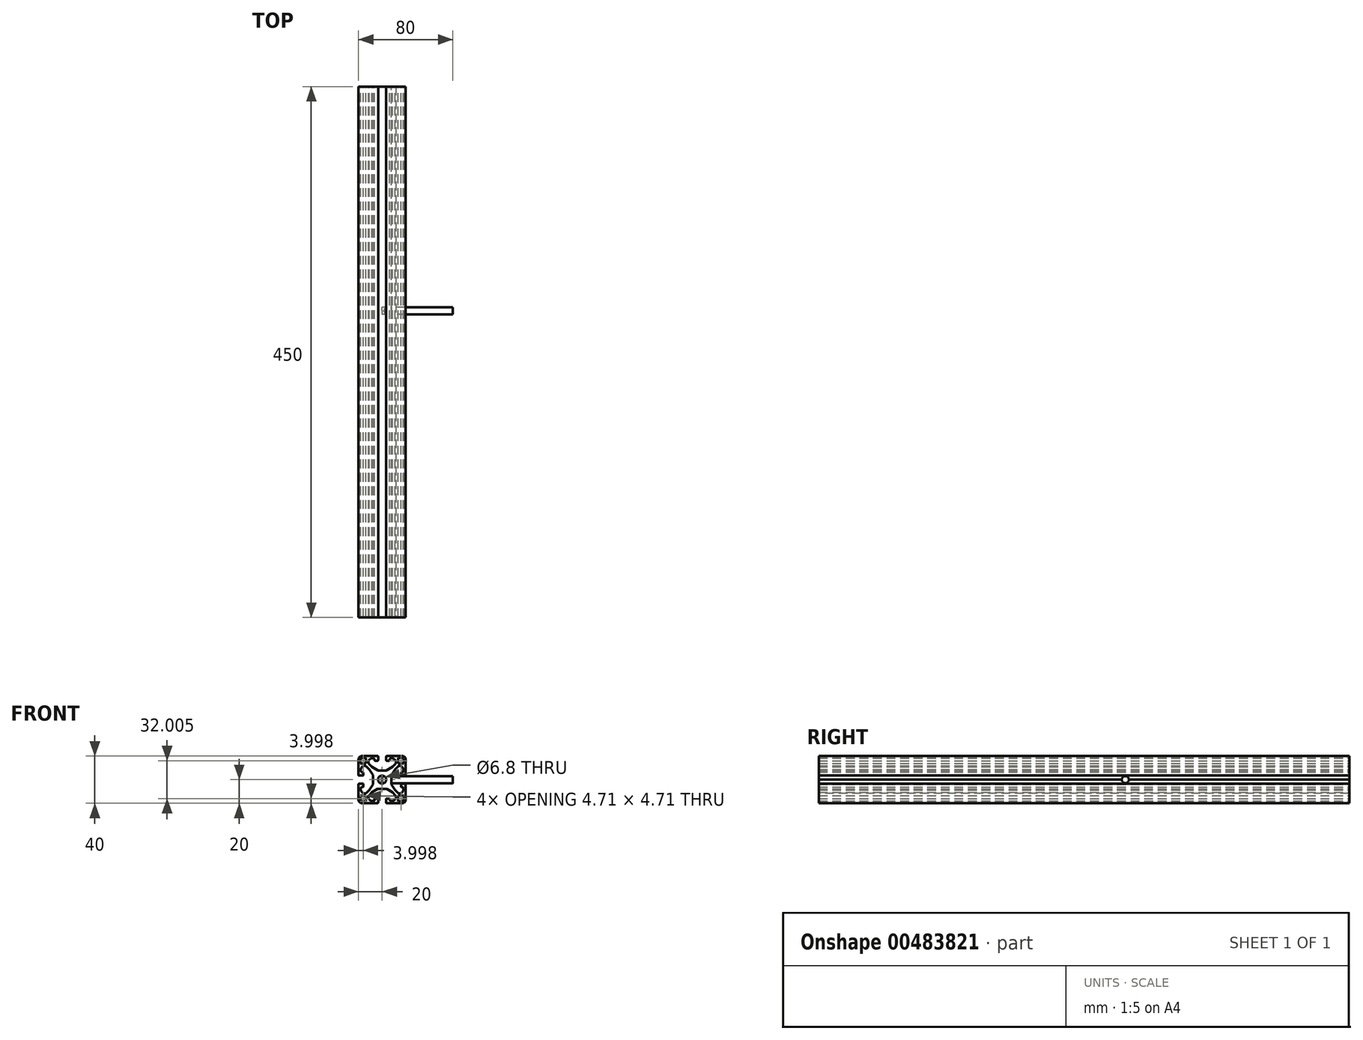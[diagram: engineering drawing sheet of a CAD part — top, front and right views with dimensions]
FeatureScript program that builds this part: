
annotation { "Feature Type Name" : "Feature", "Feature Type Description" : "" }
export const myFeature = defineFeature(function(context is Context, id is Id, definition is map)
    precondition{}
    {
        {
            var Q0;
            Q0=qCreatedBy(makeId("Front.planeOp"),FACE);
            var sketch = newSketch(context, id + "F0", { "sketchPlane" : qUnion([Q0])});
            skLineSegment(sketch, "E0.bottom", {"start": v(-16.36, 18.36) * mm, "end": v(-13.65, 18.36) * mm});
            skLineSegment(sketch, "E0.top", {"start": v(-18.36, 13.65) * mm, "end": v(-13.65, 13.65) * mm});
            skLineSegment(sketch, "E0.left", {"start": v(-18.36, 18.36) * mm, "end": v(-18.36, 18.36) * mm});
            skLineSegment(sketch, "E0.right", {"start": v(-13.65, 18.36) * mm, "end": v(-13.65, 13.65) * mm});
            skLineSegment(sketch, "E1", {"start": v(-7.83, 4) * mm, "end": v(-10.88, 8.69) * mm});
            skLineSegment(sketch, "E2", {"start": v(-10.88, 8.69) * mm, "end": v(-13.5, 11.3) * mm});
            skCircle(sketch, "E3", {"center": v(0, 0) * mm, "radius": 3.4 * mm});
            skLineSegment(sketch, "E4", {"start": v(-20, 3.4) * mm, "end": v(-19.97, 3.4) * mm});
            skLineSegment(sketch, "E5", {"start": v(-16, 3.9) * mm, "end": v(-16, 5.9) * mm});
            skLineSegment(sketch, "E6", {"start": v(-16.5, 6.4) * mm, "end": v(-17.08, 6.4) * mm});
            skFitSpline(sketch, "E7", {"points": [v(-18, 6.4) * mm, v(-18, 9.03) * mm, v(-17.04, 10.7) * mm, v(-15.02, 11.66) * mm, v(-13.85, 11.66) * mm, v(-51.55, 27.96) * mm, v(-53, 27.74) * mm], "startDerivative": vector(-2.1, 22.69) * mm, "endDerivative": vector(-5.98, -7.44) * mm});
            skArc(sketch, "E8.filletArc", {"start": v(-18.08, 7.34) * mm, "mid": v(-17.76, 6.67) * mm, "end": v(-17.08, 6.4) * mm});
            skArc(sketch, "E9.filletArc", {"start": v(-13.5, 11.3) * mm, "mid": v(-13.78, 11.5) * mm, "end": v(-14.1, 11.6) * mm});
            skLineSegment(sketch, "E10", {"start": v(-18.36, 16.36) * mm, "end": v(-18.36, 13.65) * mm});
            skPoint(sketch, "E11.visualSharp", {"position": v(-16, 6.4) * mm});
            skArc(sketch, "E11.filletArc", {"start": v(-16, 5.9) * mm, "mid": v(-16.15, 6.25) * mm, "end": v(-16.5, 6.4) * mm});
            skPoint(sketch, "E12.visualSharp", {"position": v(-16, 3.4) * mm});
            skArc(sketch, "E12.filletArc", {"start": v(-16.5, 3.4) * mm, "mid": v(-16.15, 3.55) * mm, "end": v(-16, 3.9) * mm});
            skLineSegment(sketch, "E13", {"start": v(-20, 3.9) * mm, "end": v(-20, 17) * mm});
            skArc(sketch, "E14.filletArc", {"start": v(-20, 3.9) * mm, "mid": v(-19.85, 3.55) * mm, "end": v(-19.5, 3.4) * mm});
            skLineSegment(sketch, "E15", {"start": v(-19.5, 3.4) * mm, "end": v(-16.5, 3.4) * mm});
            skPoint(sketch, "E16.visualSharp", {"position": v(-7.75, 3.88) * mm});
            skArc(sketch, "E16.filletArc", {"start": v(-7.75, 3.73) * mm, "mid": v(-7.77, 3.87) * mm, "end": v(-7.83, 4) * mm});
            skPoint(sketch, "E17.visualSharp", {"position": v(-18.36, 18.36) * mm});
            skArc(sketch, "E17.filletArc", {"start": v(-16.36, 18.36) * mm, "mid": v(-17.77, 17.77) * mm, "end": v(-18.36, 16.36) * mm});
            skPoint(sketch, "E18.visualSharp", {"position": v(-20, 20) * mm});
            skArc(sketch, "E18.filletArc", {"start": v(-17, 20) * mm, "mid": v(-19.12, 19.12) * mm, "end": v(-20, 17) * mm});
            skArc(sketch, "E19.MirrorCS", {"start": v(-7.34, 18.08) * mm, "mid": v(-6.67, 17.76) * mm, "end": v(-6.4, 17.08) * mm});
            skLineSegment(sketch, "E20.MirrorCS", {"start": v(-6.4, 16.5) * mm, "end": v(-6.4, 17.08) * mm});
            skLineSegment(sketch, "E21.MirrorCS", {"start": v(-3.9, 16) * mm, "end": v(-5.9, 16) * mm});
            skArc(sketch, "E22.MirrorCS", {"start": v(-5.9, 16) * mm, "mid": v(-6.25, 16.15) * mm, "end": v(-6.4, 16.5) * mm});
            skArc(sketch, "E23.MirrorCS", {"start": v(-11.3, 13.5) * mm, "mid": v(-11.5, 13.78) * mm, "end": v(-11.6, 14.1) * mm});
            skArc(sketch, "E24.MirrorCS", {"start": v(-3.73, 7.75) * mm, "mid": v(-3.87, 7.77) * mm, "end": v(-4, 7.83) * mm});
            skArc(sketch, "E25.MirrorCS", {"start": v(-3.4, 16.5) * mm, "mid": v(-3.55, 16.15) * mm, "end": v(-3.9, 16) * mm});
            skLineSegment(sketch, "E26.MirrorCS", {"start": v(-3.4, 19.5) * mm, "end": v(-3.4, 16.5) * mm});
            skLineSegment(sketch, "E27.MirrorCS", {"start": v(-3.4, 20) * mm, "end": v(-3.4, 19.97) * mm});
            skArc(sketch, "E28.MirrorCS", {"start": v(-3.9, 20) * mm, "mid": v(-3.55, 19.85) * mm, "end": v(-3.4, 19.5) * mm});
            skLineSegment(sketch, "E29.MirrorCS", {"start": v(-8.69, 10.88) * mm, "end": v(-11.3, 13.5) * mm});
            skArc(sketch, "E30.MirrorCS", {"start": v(-20, 17) * mm, "mid": v(-19.12, 19.12) * mm, "end": v(-17, 20) * mm});
            skArc(sketch, "E31.MirrorCS", {"start": v(-18.36, 16.36) * mm, "mid": v(-17.77, 17.77) * mm, "end": v(-16.36, 18.36) * mm});
            skFitSpline(sketch, "E32.MirrorCS", {"points": [v(-6.4, 18) * mm, v(-9.03, 18) * mm, v(-10.7, 17.04) * mm, v(-11.66, 15.02) * mm, v(-11.66, 13.85) * mm, v(-27.96, 51.55) * mm, v(-27.74, 53) * mm], "startDerivative": vector(-22.69, 2.1) * mm, "endDerivative": vector(7.44, 5.98) * mm});
            skPoint(sketch, "E33.MirrorP", {"position": v(-6.4, 16) * mm});
            skPoint(sketch, "E34.MirrorP", {"position": v(-3.88, 7.75) * mm});
            skPoint(sketch, "E35.MirrorP", {"position": v(-3.4, 16) * mm});
            skLineSegment(sketch, "E36.MirrorCS", {"start": v(-3.9, 20) * mm, "end": v(-17, 20) * mm});
            skLineSegment(sketch, "E37.MirrorCS", {"start": v(-4, 7.83) * mm, "end": v(-8.69, 10.88) * mm});
            skLineSegment(sketch, "E38.MirrorCS", {"start": v(0, 7.75) * mm, "end": v(-3.73, 7.75) * mm});
            skArc(sketch, "E39.MirrorCS", {"start": v(18.36, 16.36) * mm, "mid": v(17.77, 17.77) * mm, "end": v(16.36, 18.36) * mm});
            skLineSegment(sketch, "E40.MirrorCS", {"start": v(16.5, 6.4) * mm, "end": v(17.08, 6.4) * mm});
            skArc(sketch, "E41.MirrorCS", {"start": v(16.36, 18.36) * mm, "mid": v(17.77, 17.77) * mm, "end": v(18.36, 16.36) * mm});
            skArc(sketch, "E42.MirrorCS", {"start": v(16, 5.9) * mm, "mid": v(16.15, 6.25) * mm, "end": v(16.5, 6.4) * mm});
            skArc(sketch, "E43.MirrorCS", {"start": v(3.73, 7.75) * mm, "mid": v(3.87, 7.77) * mm, "end": v(4, 7.83) * mm});
            skPoint(sketch, "E44.MirrorP", {"position": v(18.36, 18.36) * mm});
            skArc(sketch, "E45.MirrorCS", {"start": v(13.5, 11.3) * mm, "mid": v(13.78, 11.5) * mm, "end": v(14.1, 11.6) * mm});
            skArc(sketch, "E46.MirrorCS", {"start": v(20, 3.9) * mm, "mid": v(19.85, 3.55) * mm, "end": v(19.5, 3.4) * mm});
            skArc(sketch, "E47.MirrorCS", {"start": v(7.75, 3.73) * mm, "mid": v(7.77, 3.87) * mm, "end": v(7.83, 4) * mm});
            skLineSegment(sketch, "E48.MirrorCS", {"start": v(16, 3.9) * mm, "end": v(16, 5.9) * mm});
            skArc(sketch, "E49.MirrorCS", {"start": v(3.4, 16.5) * mm, "mid": v(3.55, 16.15) * mm, "end": v(3.9, 16) * mm});
            skArc(sketch, "E50.MirrorCS", {"start": v(5.9, 16) * mm, "mid": v(6.25, 16.15) * mm, "end": v(6.4, 16.5) * mm});
            skArc(sketch, "E51.MirrorCS", {"start": v(18.08, 7.34) * mm, "mid": v(17.76, 6.67) * mm, "end": v(17.08, 6.4) * mm});
            skLineSegment(sketch, "E52.MirrorCS", {"start": v(3.9, 16) * mm, "end": v(5.9, 16) * mm});
            skArc(sketch, "E53.MirrorCS", {"start": v(16.5, 3.4) * mm, "mid": v(16.15, 3.55) * mm, "end": v(16, 3.9) * mm});
            skArc(sketch, "E54.MirrorCS", {"start": v(11.3, 13.5) * mm, "mid": v(11.5, 13.78) * mm, "end": v(11.6, 14.1) * mm});
            skLineSegment(sketch, "E55.MirrorCS", {"start": v(20, 3.4) * mm, "end": v(19.97, 3.4) * mm});
            skLineSegment(sketch, "E56.MirrorCS", {"start": v(6.4, 16.5) * mm, "end": v(6.4, 17.08) * mm});
            skArc(sketch, "E57.MirrorCS", {"start": v(3.9, 20) * mm, "mid": v(3.55, 19.85) * mm, "end": v(3.4, 19.5) * mm});
            skLineSegment(sketch, "E58.MirrorCS", {"start": v(3.4, 20) * mm, "end": v(3.4, 19.97) * mm});
            skArc(sketch, "E59.MirrorCS", {"start": v(7.34, 18.08) * mm, "mid": v(6.67, 17.76) * mm, "end": v(6.4, 17.08) * mm});
            skPoint(sketch, "E60.MirrorP", {"position": v(16, 6.4) * mm});
            skArc(sketch, "E61.MirrorCS", {"start": v(20, 17) * mm, "mid": v(19.12, 19.12) * mm, "end": v(17, 20) * mm});
            skPoint(sketch, "E62.MirrorP", {"position": v(20, 20) * mm});
            skFitSpline(sketch, "E63.MirrorCS", {"points": [v(6.4, 18) * mm, v(9.03, 18) * mm, v(10.7, 17.04) * mm, v(11.66, 15.02) * mm, v(11.66, 13.85) * mm, v(27.96, 51.55) * mm, v(27.74, 53) * mm], "startDerivative": vector(22.69, 2.1) * mm, "endDerivative": vector(-7.44, 5.98) * mm});
            skLineSegment(sketch, "E64.MirrorCS", {"start": v(18.36, 13.65) * mm, "end": v(13.65, 13.65) * mm});
            skLineSegment(sketch, "E65.MirrorCS", {"start": v(18.36, 18.36) * mm, "end": v(18.36, 18.36) * mm});
            skFitSpline(sketch, "E66.MirrorCS", {"points": [v(18, 6.4) * mm, v(18, 9.03) * mm, v(17.04, 10.7) * mm, v(15.02, 11.66) * mm, v(13.85, 11.66) * mm, v(51.55, 27.96) * mm, v(53, 27.74) * mm], "startDerivative": vector(2.1, 22.69) * mm, "endDerivative": vector(5.98, -7.44) * mm});
            skLineSegment(sketch, "E67.MirrorCS", {"start": v(16.36, 18.36) * mm, "end": v(13.65, 18.36) * mm});
            skLineSegment(sketch, "E68.MirrorCS", {"start": v(13.65, 18.36) * mm, "end": v(13.65, 13.65) * mm});
            skLineSegment(sketch, "E69.MirrorCS", {"start": v(19.5, 3.4) * mm, "end": v(16.5, 3.4) * mm});
            skLineSegment(sketch, "E70.MirrorCS", {"start": v(18.36, 16.36) * mm, "end": v(18.36, 13.65) * mm});
            skPoint(sketch, "E71.MirrorP", {"position": v(16, 3.4) * mm});
            skPoint(sketch, "E72.MirrorP", {"position": v(3.4, 16) * mm});
            skLineSegment(sketch, "E73.MirrorCS", {"start": v(8.69, 10.88) * mm, "end": v(11.3, 13.5) * mm});
            skArc(sketch, "E74.MirrorCS", {"start": v(17, 20) * mm, "mid": v(19.12, 19.12) * mm, "end": v(20, 17) * mm});
            skLineSegment(sketch, "E75.MirrorCS", {"start": v(3.4, 19.5) * mm, "end": v(3.4, 16.5) * mm});
            skPoint(sketch, "E76.MirrorP", {"position": v(7.75, 3.88) * mm});
            skPoint(sketch, "E77.MirrorP", {"position": v(3.88, 7.75) * mm});
            skLineSegment(sketch, "E78.MirrorCS", {"start": v(20, 3.9) * mm, "end": v(20, 17) * mm});
            skLineSegment(sketch, "E79.MirrorCS", {"start": v(0, 7.75) * mm, "end": v(3.73, 7.75) * mm});
            skLineSegment(sketch, "E80.MirrorCS", {"start": v(4, 7.83) * mm, "end": v(8.69, 10.88) * mm});
            skLineSegment(sketch, "E81.MirrorCS", {"start": v(7.83, 4) * mm, "end": v(10.88, 8.69) * mm});
            skLineSegment(sketch, "E82.MirrorCS", {"start": v(3.9, 20) * mm, "end": v(17, 20) * mm});
            skLineSegment(sketch, "E83.MirrorCS", {"start": v(7.75, 0) * mm, "end": v(7.75, 3.73) * mm});
            skLineSegment(sketch, "E84.MirrorCS", {"start": v(10.88, 8.69) * mm, "end": v(13.5, 11.3) * mm});
            skPoint(sketch, "E85.MirrorP", {"position": v(6.4, 16) * mm});
            skLineSegment(sketch, "E86.MirrorCS", {"start": v(18.36, -16.36) * mm, "end": v(18.36, -13.65) * mm});
            skLineSegment(sketch, "E87.MirrorCS", {"start": v(16.36, -18.36) * mm, "end": v(13.65, -18.36) * mm});
            skArc(sketch, "E88.MirrorCS", {"start": v(18.36, -16.36) * mm, "mid": v(17.77, -17.77) * mm, "end": v(16.36, -18.36) * mm});
            skLineSegment(sketch, "E89.MirrorCS", {"start": v(-16.36, -18.36) * mm, "end": v(-13.65, -18.36) * mm});
            skArc(sketch, "E90.MirrorCS", {"start": v(20, -17) * mm, "mid": v(19.12, -19.12) * mm, "end": v(17, -20) * mm});
            skLineSegment(sketch, "E91.MirrorCS", {"start": v(-18.36, -16.36) * mm, "end": v(-18.36, -13.65) * mm});
            skArc(sketch, "E92.MirrorCS", {"start": v(-20, -17) * mm, "mid": v(-19.12, -19.12) * mm, "end": v(-17, -20) * mm});
            skArc(sketch, "E93.MirrorCS", {"start": v(-18.36, -16.36) * mm, "mid": v(-17.77, -17.77) * mm, "end": v(-16.36, -18.36) * mm});
            skArc(sketch, "E94.MirrorCS", {"start": v(13.5, -11.3) * mm, "mid": v(13.78, -11.5) * mm, "end": v(14.1, -11.6) * mm});
            skArc(sketch, "E95.MirrorCS", {"start": v(-18.08, -7.34) * mm, "mid": v(-17.76, -6.67) * mm, "end": v(-17.08, -6.4) * mm});
            skArc(sketch, "E96.MirrorCS", {"start": v(3.73, -7.75) * mm, "mid": v(3.87, -7.77) * mm, "end": v(4, -7.83) * mm});
            skLineSegment(sketch, "E97.MirrorCS", {"start": v(-16.5, -6.4) * mm, "end": v(-17.08, -6.4) * mm});
            skArc(sketch, "E98.MirrorCS", {"start": v(16.36, -18.36) * mm, "mid": v(17.77, -17.77) * mm, "end": v(18.36, -16.36) * mm});
            skArc(sketch, "E99.MirrorCS", {"start": v(-16.36, -18.36) * mm, "mid": v(-17.77, -17.77) * mm, "end": v(-18.36, -16.36) * mm});
            skArc(sketch, "E100.MirrorCS", {"start": v(-3.73, -7.75) * mm, "mid": v(-3.87, -7.77) * mm, "end": v(-4, -7.83) * mm});
            skArc(sketch, "E101.MirrorCS", {"start": v(-16, -5.9) * mm, "mid": v(-16.15, -6.25) * mm, "end": v(-16.5, -6.4) * mm});
            skArc(sketch, "E102.MirrorCS", {"start": v(17, -20) * mm, "mid": v(19.12, -19.12) * mm, "end": v(20, -17) * mm});
            skArc(sketch, "E103.MirrorCS", {"start": v(-17, -20) * mm, "mid": v(-19.12, -19.12) * mm, "end": v(-20, -17) * mm});
            skArc(sketch, "E104.MirrorCS", {"start": v(-13.5, -11.3) * mm, "mid": v(-13.78, -11.5) * mm, "end": v(-14.1, -11.6) * mm});
            skArc(sketch, "E105.MirrorCS", {"start": v(-5.9, -16) * mm, "mid": v(-6.25, -16.15) * mm, "end": v(-6.4, -16.5) * mm});
            skLineSegment(sketch, "E106.MirrorCS", {"start": v(-3.9, -16) * mm, "end": v(-5.9, -16) * mm});
            skArc(sketch, "E107.MirrorCS", {"start": v(7.34, -18.08) * mm, "mid": v(6.67, -17.76) * mm, "end": v(6.4, -17.08) * mm});
            skLineSegment(sketch, "E108.MirrorCS", {"start": v(-6.4, -16.5) * mm, "end": v(-6.4, -17.08) * mm});
            skArc(sketch, "E109.MirrorCS", {"start": v(16, -5.9) * mm, "mid": v(16.15, -6.25) * mm, "end": v(16.5, -6.4) * mm});
            skLineSegment(sketch, "E110.MirrorCS", {"start": v(-16, -3.9) * mm, "end": v(-16, -5.9) * mm});
            skLineSegment(sketch, "E111.MirrorCS", {"start": v(-20, -3.4) * mm, "end": v(-19.97, -3.4) * mm});
            skArc(sketch, "E112.MirrorCS", {"start": v(-7.34, -18.08) * mm, "mid": v(-6.67, -17.76) * mm, "end": v(-6.4, -17.08) * mm});
            skArc(sketch, "E113.MirrorCS", {"start": v(-16.5, -3.4) * mm, "mid": v(-16.15, -3.55) * mm, "end": v(-16, -3.9) * mm});
            skArc(sketch, "E114.MirrorCS", {"start": v(-3.4, -16.5) * mm, "mid": v(-3.55, -16.15) * mm, "end": v(-3.9, -16) * mm});
            skArc(sketch, "E115.MirrorCS", {"start": v(7.75, -3.73) * mm, "mid": v(7.77, -3.87) * mm, "end": v(7.83, -4) * mm});
            skArc(sketch, "E116.MirrorCS", {"start": v(-20, -3.9) * mm, "mid": v(-19.85, -3.55) * mm, "end": v(-19.5, -3.4) * mm});
            skLineSegment(sketch, "E117.MirrorCS", {"start": v(6.4, -16.5) * mm, "end": v(6.4, -17.08) * mm});
            skArc(sketch, "E118.MirrorCS", {"start": v(5.9, -16) * mm, "mid": v(6.25, -16.15) * mm, "end": v(6.4, -16.5) * mm});
            skLineSegment(sketch, "E119.MirrorCS", {"start": v(16, -3.9) * mm, "end": v(16, -5.9) * mm});
            skLineSegment(sketch, "E120.MirrorCS", {"start": v(-19.5, -3.4) * mm, "end": v(-16.5, -3.4) * mm});
            skArc(sketch, "E121.MirrorCS", {"start": v(18.08, -7.34) * mm, "mid": v(17.76, -6.67) * mm, "end": v(17.08, -6.4) * mm});
            skPoint(sketch, "E122.MirrorP", {"position": v(18.36, -18.36) * mm});
            skLineSegment(sketch, "E123.MirrorCS", {"start": v(3.9, -16) * mm, "end": v(5.9, -16) * mm});
            skArc(sketch, "E124.MirrorCS", {"start": v(-11.3, -13.5) * mm, "mid": v(-11.5, -13.78) * mm, "end": v(-11.6, -14.1) * mm});
            skPoint(sketch, "E125.MirrorP", {"position": v(-18.36, -18.36) * mm});
            skLineSegment(sketch, "E126.MirrorCS", {"start": v(-3.4, -20) * mm, "end": v(-3.4, -19.97) * mm});
            skArc(sketch, "E127.MirrorCS", {"start": v(11.3, -13.5) * mm, "mid": v(11.5, -13.78) * mm, "end": v(11.6, -14.1) * mm});
            skArc(sketch, "E128.MirrorCS", {"start": v(16.5, -3.4) * mm, "mid": v(16.15, -3.55) * mm, "end": v(16, -3.9) * mm});
            skArc(sketch, "E129.MirrorCS", {"start": v(-7.75, -3.73) * mm, "mid": v(-7.77, -3.87) * mm, "end": v(-7.83, -4) * mm});
            skLineSegment(sketch, "E130.MirrorCS", {"start": v(16.5, -6.4) * mm, "end": v(17.08, -6.4) * mm});
            skArc(sketch, "E131.MirrorCS", {"start": v(3.4, -16.5) * mm, "mid": v(3.55, -16.15) * mm, "end": v(3.9, -16) * mm});
            skLineSegment(sketch, "E132.MirrorCS", {"start": v(3.4, -20) * mm, "end": v(3.4, -19.97) * mm});
            skLineSegment(sketch, "E133.MirrorCS", {"start": v(-10.88, -8.69) * mm, "end": v(-13.5, -11.3) * mm});
            skArc(sketch, "E134.MirrorCS", {"start": v(3.9, -20) * mm, "mid": v(3.55, -19.85) * mm, "end": v(3.4, -19.5) * mm});
            skLineSegment(sketch, "E135.MirrorCS", {"start": v(19.5, -3.4) * mm, "end": v(16.5, -3.4) * mm});
            skArc(sketch, "E136.MirrorCS", {"start": v(-3.9, -20) * mm, "mid": v(-3.55, -19.85) * mm, "end": v(-3.4, -19.5) * mm});
            skLineSegment(sketch, "E137.MirrorCS", {"start": v(-13.65, -18.36) * mm, "end": v(-13.65, -13.65) * mm});
            skLineSegment(sketch, "E138.MirrorCS", {"start": v(-3.4, -19.5) * mm, "end": v(-3.4, -16.5) * mm});
            skLineSegment(sketch, "E139.MirrorCS", {"start": v(10.88, -8.69) * mm, "end": v(13.5, -11.3) * mm});
            skLineSegment(sketch, "E140.MirrorCS", {"start": v(20, -3.4) * mm, "end": v(19.97, -3.4) * mm});
            skLineSegment(sketch, "E141.MirrorCS", {"start": v(3.4, -19.5) * mm, "end": v(3.4, -16.5) * mm});
            skArc(sketch, "E142.MirrorCS", {"start": v(20, -3.9) * mm, "mid": v(19.85, -3.55) * mm, "end": v(19.5, -3.4) * mm});
            skLineSegment(sketch, "E143.MirrorCS", {"start": v(7.83, -4) * mm, "end": v(10.88, -8.69) * mm});
            skFitSpline(sketch, "E144.MirrorCS", {"points": [v(-18, -6.4) * mm, v(-18, -9.03) * mm, v(-17.04, -10.7) * mm, v(-15.02, -11.66) * mm, v(-13.85, -11.66) * mm, v(-51.55, -27.96) * mm, v(-53, -27.74) * mm], "startDerivative": vector(-2.1, -22.69) * mm, "endDerivative": vector(-5.98, 7.44) * mm});
            skLineSegment(sketch, "E145.MirrorCS", {"start": v(18.36, -18.36) * mm, "end": v(18.36, -18.36) * mm});
            skLineSegment(sketch, "E146.MirrorCS", {"start": v(-18.36, -13.65) * mm, "end": v(-13.65, -13.65) * mm});
            skFitSpline(sketch, "E147.MirrorCS", {"points": [v(-6.4, -18) * mm, v(-9.03, -18) * mm, v(-10.7, -17.04) * mm, v(-11.66, -15.02) * mm, v(-11.66, -13.85) * mm, v(-27.96, -51.55) * mm, v(-27.74, -53) * mm], "startDerivative": vector(-22.69, -2.1) * mm, "endDerivative": vector(7.44, -5.98) * mm});
            skLineSegment(sketch, "E148.MirrorCS", {"start": v(18.36, -13.65) * mm, "end": v(13.65, -13.65) * mm});
            skFitSpline(sketch, "E149.MirrorCS", {"points": [v(18, -6.4) * mm, v(18, -9.03) * mm, v(17.04, -10.7) * mm, v(15.02, -11.66) * mm, v(13.85, -11.66) * mm, v(51.55, -27.96) * mm, v(53, -27.74) * mm], "startDerivative": vector(2.1, -22.69) * mm, "endDerivative": vector(5.98, 7.44) * mm});
            skPoint(sketch, "E150.MirrorP", {"position": v(20, -20) * mm});
            skLineSegment(sketch, "E151.MirrorCS", {"start": v(-8.69, -10.88) * mm, "end": v(-11.3, -13.5) * mm});
            skLineSegment(sketch, "E152.MirrorCS", {"start": v(-18.36, -18.36) * mm, "end": v(-18.36, -18.36) * mm});
            skPoint(sketch, "E153.MirrorP", {"position": v(-20, -20) * mm});
            skFitSpline(sketch, "E154.MirrorCS", {"points": [v(6.4, -18) * mm, v(9.03, -18) * mm, v(10.7, -17.04) * mm, v(11.66, -15.02) * mm, v(11.66, -13.85) * mm, v(27.96, -51.55) * mm, v(27.74, -53) * mm], "startDerivative": vector(22.69, -2.1) * mm, "endDerivative": vector(-7.44, -5.98) * mm});
            skLineSegment(sketch, "E155.MirrorCS", {"start": v(0, -7.75) * mm, "end": v(-3.73, -7.75) * mm});
            skLineSegment(sketch, "E156.MirrorCS", {"start": v(-20, -3.9) * mm, "end": v(-20, -17) * mm});
            skLineSegment(sketch, "E157.MirrorCS", {"start": v(-3.9, -20) * mm, "end": v(-17, -20) * mm});
            skPoint(sketch, "E158.MirrorP", {"position": v(-16, -6.4) * mm});
            skLineSegment(sketch, "E159.MirrorCS", {"start": v(13.65, -18.36) * mm, "end": v(13.65, -13.65) * mm});
            skLineSegment(sketch, "E160.MirrorCS", {"start": v(8.69, -10.88) * mm, "end": v(11.3, -13.5) * mm});
            skLineSegment(sketch, "E161.MirrorCS", {"start": v(3.9, -20) * mm, "end": v(17, -20) * mm});
            skPoint(sketch, "E162.MirrorP", {"position": v(16, -3.4) * mm});
            skLineSegment(sketch, "E163.MirrorCS", {"start": v(4, -7.83) * mm, "end": v(8.69, -10.88) * mm});
            skLineSegment(sketch, "E164.MirrorCS", {"start": v(-7.83, -4) * mm, "end": v(-10.88, -8.69) * mm});
            skPoint(sketch, "E165.MirrorP", {"position": v(16, -6.4) * mm});
            skPoint(sketch, "E166.MirrorP", {"position": v(3.4, -16) * mm});
            skPoint(sketch, "E167.MirrorP", {"position": v(-3.88, -7.75) * mm});
            skLineSegment(sketch, "E168.MirrorCS", {"start": v(20, -3.9) * mm, "end": v(20, -17) * mm});
            skPoint(sketch, "E169.MirrorP", {"position": v(6.4, -16) * mm});
            skPoint(sketch, "E170.MirrorP", {"position": v(3.88, -7.75) * mm});
            skPoint(sketch, "E171.MirrorP", {"position": v(-7.75, -3.88) * mm});
            skLineSegment(sketch, "E172.MirrorCS", {"start": v(-4, -7.83) * mm, "end": v(-8.69, -10.88) * mm});
            skPoint(sketch, "E173.MirrorP", {"position": v(7.75, -3.88) * mm});
            skPoint(sketch, "E174.MirrorP", {"position": v(-3.4, -16) * mm});
            skPoint(sketch, "E175.MirrorP", {"position": v(-6.4, -16) * mm});
            skPoint(sketch, "E176.MirrorP", {"position": v(-16, -3.4) * mm});
            skLineSegment(sketch, "E177", {"start": v(-7.75, -3.73) * mm, "end": v(-7.75, 3.73) * mm});
            skLineSegment(sketch, "E178", {"start": v(0, -7.75) * mm, "end": v(3.88, -7.75) * mm});
            skLineSegment(sketch, "E179", {"start": v(7.83, -4) * mm, "end": v(7.75, 0) * mm});
            skSolve(sketch);
        }
        {
            var Q0;
            Q0 = qSketchRegion(id + "F0", true);
            extrude(context, id + "F1", {"entities" : qUnion([Q0]), "depth" : 450 * mm});
        }
        {
            var Q0;
            Q0=qCreatedBy(makeId("Right.planeOp"),FACE);
            var sketch = newSketch(context, id + "F2", { "sketchPlane" : qUnion([Q0])});
            skLineSegment(sketch, "E180", {"start": v(0, 0) * mm, "end": v(-190, 0) * mm});
            skCircle(sketch, "E181", {"center": v(-190, 0) * mm, "radius": 3 * mm});
            skSolve(sketch);
        }
        {
            var Q0;
            Q0 = qSketchRegion(id + "F2", true);
            extrude(context, id + "F3", {"entities" : qUnion([Q0]), "operationType" : NewBodyOperationType.ADD, "depth" : 60 * mm});
        }
        {
            var Q0;
            Q0 = qSketchRegion(id + "F2", true);
            extrude(context, id + "F4", {"entities" : qUnion([Q0]), "operationType" : NewBodyOperationType.ADD, "depth" : 25.4 * mm});
        }
    });
